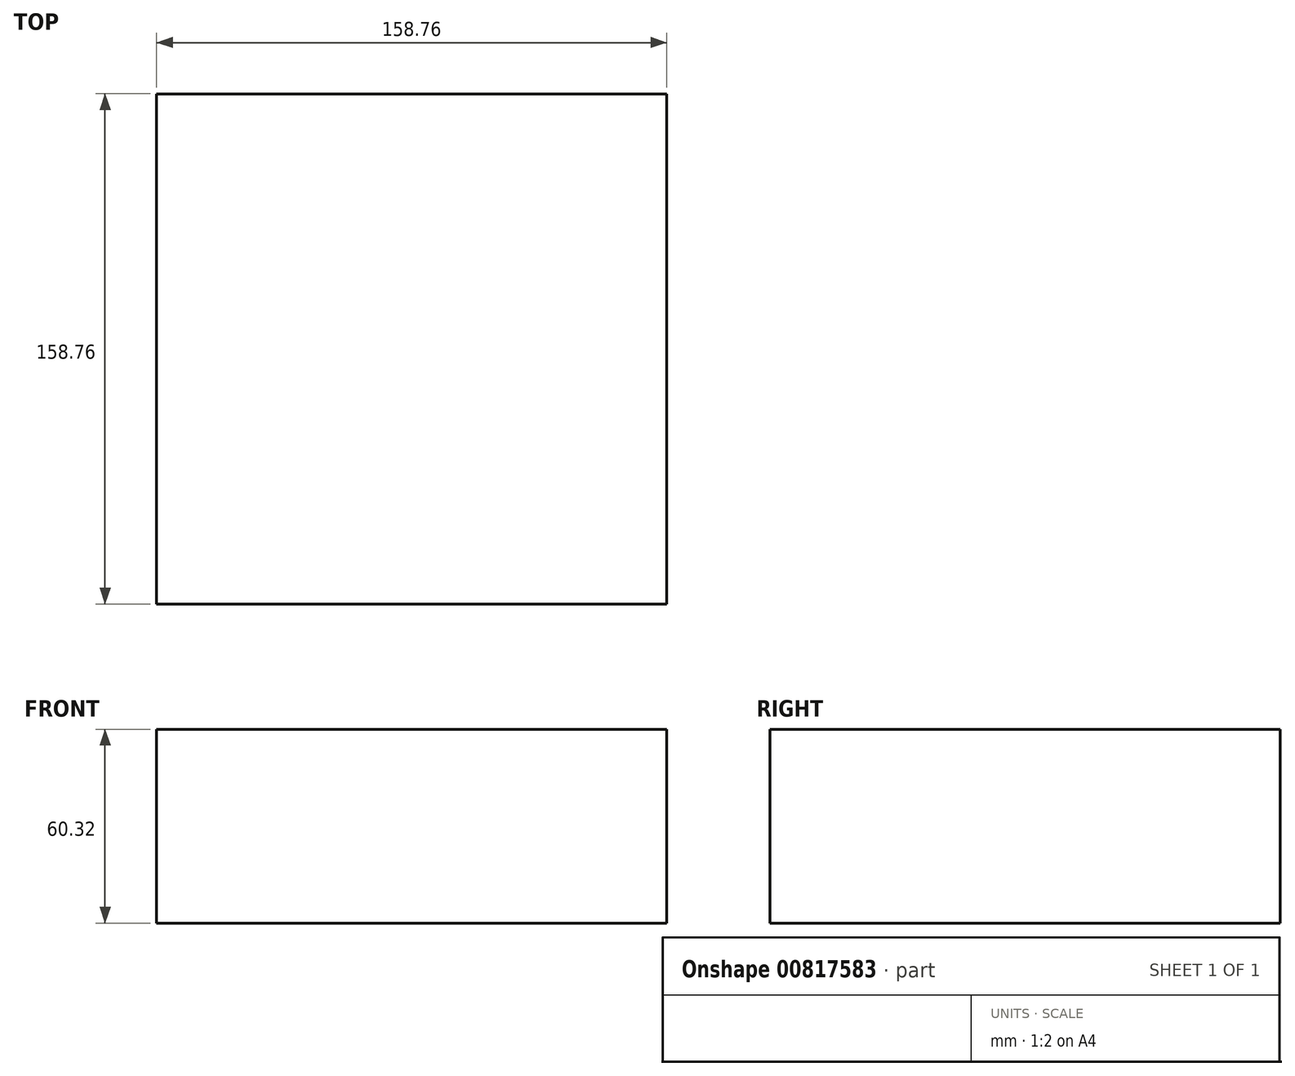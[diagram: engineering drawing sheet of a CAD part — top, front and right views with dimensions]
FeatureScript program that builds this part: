
annotation { "Feature Type Name" : "Feature", "Feature Type Description" : "" }
export const myFeature = defineFeature(function(context is Context, id is Id, definition is map)
    precondition{}
    {
        {
            var Q0;
            Q0=qCreatedBy(makeId("Top.planeOp"),FACE);
            var sketch = newSketch(context, id + "F0", { "sketchPlane" : qUnion([Q0])});
            skLineSegment(sketch, "E0.bottom", {"start": v(79.38, -79.38) * mm, "end": v(-79.37, -79.38) * mm});
            skLineSegment(sketch, "E0.top", {"start": v(79.37, 79.38) * mm, "end": v(-79.38, 79.37) * mm});
            skLineSegment(sketch, "E0.left", {"start": v(79.38, -79.38) * mm, "end": v(79.37, 79.38) * mm});
            skLineSegment(sketch, "E0.right", {"start": v(-79.37, -79.38) * mm, "end": v(-79.38, 79.38) * mm});
            skPoint(sketch, "E0.middle", {"position": v(0, 0) * mm});
            skSolve(sketch);
        }
        {
            var Q0;
            Q0=makeQuery(id+"F0.imprint","IMPRINT",FACE,{"disambiguationData":[TD([[makeQuery(id+"F0.imprint","IMPRINT",EDGE,{"derivedFrom":sQuery(id+"F0.wireOp",EDGE,"E0.bottom")}),-1.0]])]});
            extrude(context, id + "F1", {"entities" : qUnion([Q0]), "depth" : 60.32 * mm, "offsetDistance" : 25.4 * mm});
        }
    });
